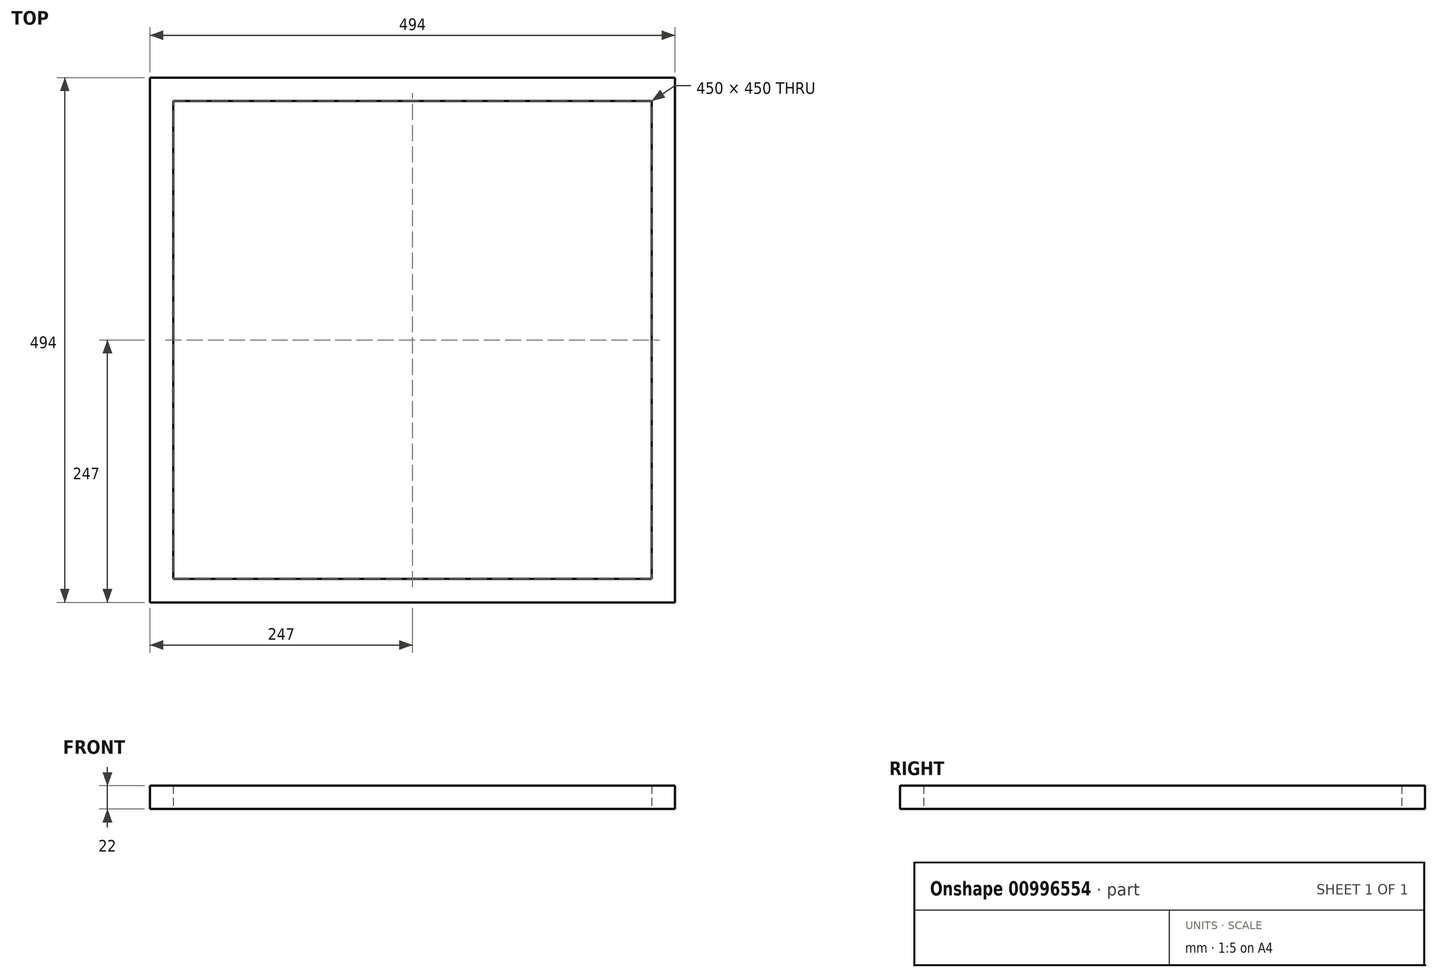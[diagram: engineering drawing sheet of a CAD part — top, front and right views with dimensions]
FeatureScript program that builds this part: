
annotation { "Feature Type Name" : "Feature", "Feature Type Description" : "" }
export const myFeature = defineFeature(function(context is Context, id is Id, definition is map)
    precondition{}
    {
        {
            assignVariable(context, id + "F0", {"name" : "aluDim", "anyValue" : 22});
        }
        {
            var Q0;
            Q0=qCreatedBy(makeId("Top.planeOp"),FACE);
            var sketch = newSketch(context, id + "F1", { "sketchPlane" : qUnion([Q0])});
            skLineSegment(sketch, "E0.bottom", {"start": v(0, 494) * mm, "end": v(494, 494) * mm});
            skLineSegment(sketch, "E0.top", {"start": v(0, 0) * mm, "end": v(494, 0) * mm});
            skLineSegment(sketch, "E0.left", {"start": v(0, 494) * mm, "end": v(0, 0) * mm});
            skLineSegment(sketch, "E0.right", {"start": v(494, 494) * mm, "end": v(494, 0) * mm});
            skLineSegment(sketch, "E1.bottom", {"start": v(22, 472) * mm, "end": v(472, 472) * mm});
            skLineSegment(sketch, "E1.top", {"start": v(22, 22) * mm, "end": v(472, 22) * mm});
            skLineSegment(sketch, "E1.left", {"start": v(22, 472) * mm, "end": v(22, 22) * mm});
            skLineSegment(sketch, "E1.right", {"start": v(472, 472) * mm, "end": v(472, 22) * mm});
            skSolve(sketch);
        }
        {
            var Q0;
            Q0=makeQuery(id+"F1.imprint","IMPRINT",FACE,{"disambiguationData":[TD([[makeQuery(id+"F1.imprint","IMPRINT",EDGE,{"derivedFrom":sQuery(id+"F1.wireOp",EDGE,"E0.bottom")}),-1.0]])]});
            extrude(context, id + "F2", {"entities" : qUnion([Q0]), "depth" : (getVariable(context, 'aluDim')) * mm, "offsetDistance" : 25 * mm});
        }
    });
